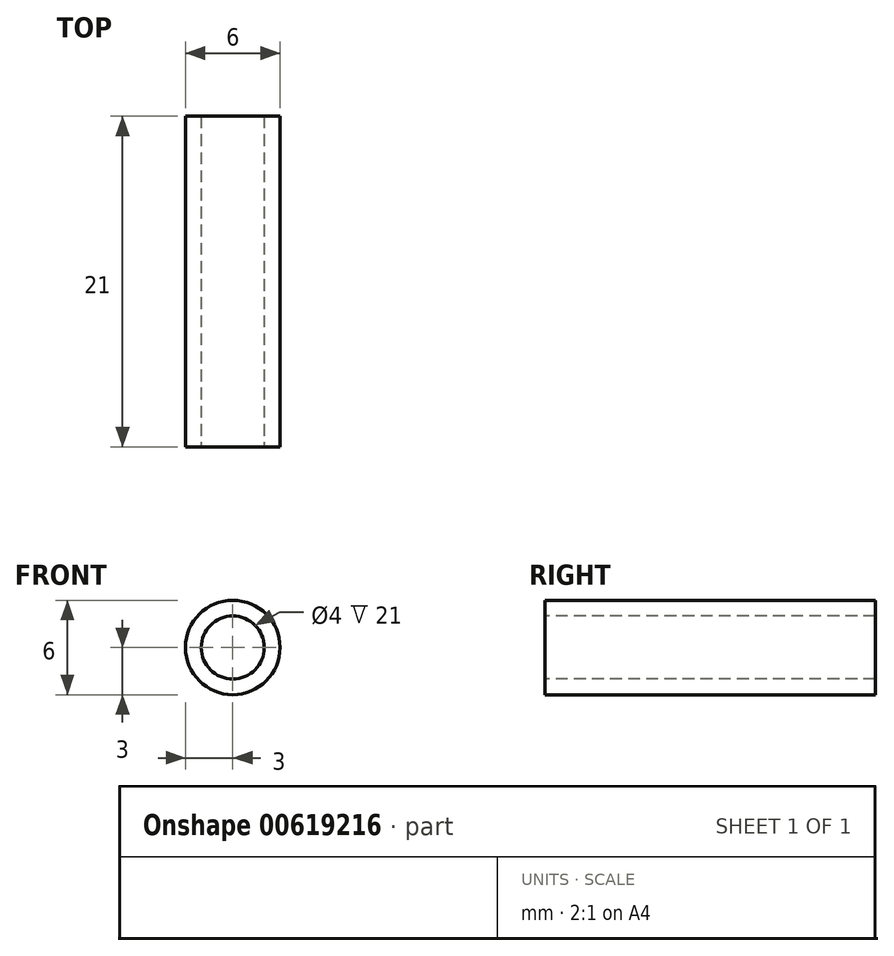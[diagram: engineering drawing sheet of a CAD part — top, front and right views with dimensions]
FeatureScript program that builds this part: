
annotation { "Feature Type Name" : "Feature", "Feature Type Description" : "" }
export const myFeature = defineFeature(function(context is Context, id is Id, definition is map)
    precondition{}
    {
        {
            var Q0;
            Q0=qCreatedBy(makeId("Front.planeOp"),FACE);
            var sketch = newSketch(context, id + "F0", { "sketchPlane" : qUnion([Q0])});
            skCircle(sketch, "E0", {"center": v(0, 0) * mm, "radius": 3 * mm});
            skSolve(sketch);
        }
        {
            var Q0;
            Q0 = qSketchRegion(id + "F0", true);
            extrude(context, id + "F1", {"entities" : qUnion([Q0]), "depth" : 21 * mm, "offsetDistance" : 25.4 * mm});
        }
        {
            var Q0;
            Q0=makeQuery(id+"F1.opExtrude","CAP_FACE",FACE,{"disambiguationData":[OSD([sQuery(id+"F0.wireOp",EDGE,"E0")])],"isStart":false});
            var sketch = newSketch(context, id + "F2", { "sketchPlane" : qUnion([Q0])});
            skCircle(sketch, "E1", {"center": v(0, 0) * mm, "radius": 2 * mm, "construction": true});
            skSolve(sketch);
        }
        {
            var Q0;
            Q0=sQuery(id+"F2.wireOp",VERTEX,"E1.center");
            var Q1;
            Q1=makeQuery(id+"F1.opExtrude","SWEPT_BODY",BODY,{"disambiguationData":[OSD([sQuery(id+"F0.wireOp",EDGE,"E0")])]});
            hole(context, id + "F3", {"style" : HoleStyle.SIMPLE, "endStyle" : HoleEndStyle.THROUGH, "holeDiameter" : 4 * mm, "majorDiameter" : 6.35 * mm, "isTappedThrough" : true, "tappedDepth" : 12.7 * mm, "tapClearance" : 3, "locations" : qUnion([Q0]), "scope" : qUnion([Q1])});
        }
    });
